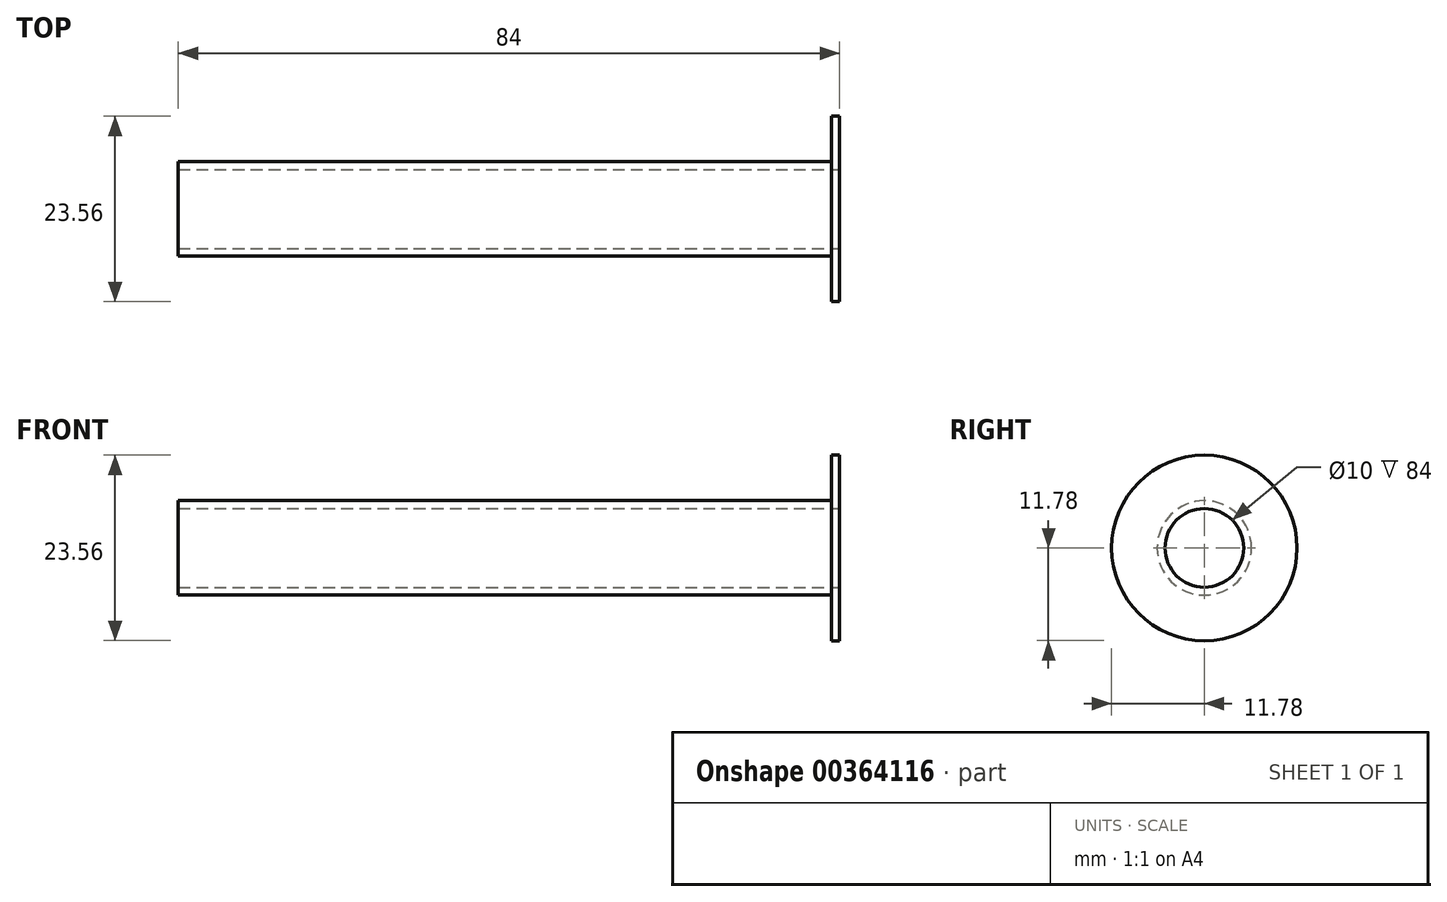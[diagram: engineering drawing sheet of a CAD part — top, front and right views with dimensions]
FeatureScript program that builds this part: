
annotation { "Feature Type Name" : "Feature", "Feature Type Description" : "" }
export const myFeature = defineFeature(function(context is Context, id is Id, definition is map)
    precondition{}
    {
        {
            var Q0;
            Q0=qCreatedBy(makeId("Front.planeOp"),FACE);
            var sketch = newSketch(context, id + "F0", { "sketchPlane" : qUnion([Q0])});
            skLineSegment(sketch, "E0.bottom", {"start": v(0, -5) * mm, "end": v(-42, -5) * mm});
            skLineSegment(sketch, "E0.top", {"start": v(0, -6) * mm, "end": v(-42, -6) * mm});
            skLineSegment(sketch, "E0.left", {"start": v(0, -5) * mm, "end": v(0, -6) * mm});
            skLineSegment(sketch, "E0.right", {"start": v(-42, -5) * mm, "end": v(-42, -6) * mm});
            skLineSegment(sketch, "E1.bottom", {"start": v(-42, -6) * mm, "end": v(-40.95, -6) * mm});
            skLineSegment(sketch, "E1.top", {"start": v(-42, -11.78) * mm, "end": v(-40.95, -11.78) * mm});
            skLineSegment(sketch, "E1.left", {"start": v(-42, -6) * mm, "end": v(-42, -11.78) * mm});
            skLineSegment(sketch, "E1.right", {"start": v(-40.95, -6) * mm, "end": v(-40.95, -11.78) * mm});
            skLineSegment(sketch, "E2.MirrorCS", {"start": v(0, -6) * mm, "end": v(42, -6) * mm});
            skLineSegment(sketch, "E3.MirrorCS", {"start": v(0, -5) * mm, "end": v(42, -5) * mm});
            skLineSegment(sketch, "E4.MirrorCS", {"start": v(42, -5) * mm, "end": v(42, -6) * mm});
            skLineSegment(sketch, "E5.MirrorCS", {"start": v(42, -6) * mm, "end": v(42, -11.78) * mm});
            skLineSegment(sketch, "E6.MirrorCS", {"start": v(40.95, -6) * mm, "end": v(40.95, -11.78) * mm});
            skLineSegment(sketch, "E7.MirrorCS", {"start": v(42, -11.78) * mm, "end": v(40.95, -11.78) * mm});
            skLineSegment(sketch, "E8", {"start": v(0, 0) * mm, "end": v(-10.68, 0) * mm, "construction": true});
            skSolve(sketch);
        }
        {
            var Q0;
            Q0=makeQuery(id+"F0.imprint","IMPRINT",FACE,{"disambiguationData":[TD([[makeQuery(id+"F0.imprint","IMPRINT",EDGE,{"derivedFrom":sQuery(id+"F0.wireOp",EDGE,"E1.bottom")}),-1.0]])]});
            var Q1;
            Q1=makeQuery(id+"F0.imprint","IMPRINT",FACE,{"disambiguationData":[TD([[makeQuery(id+"F0.imprint","IMPRINT",EDGE,{"derivedFrom":sQuery(id+"F0.wireOp",EDGE,"E0.bottom")}),1.0]])]});
            var Q2;
            {var subQ0=sQuery(id+"F0.wireOp",EDGE,"E5.MirrorCS");Q2=makeQuery(id+"F0.imprint","IMPRINT",FACE,{"disambiguationData":[TD([[makeQuery(id+"F0.imprint","IMPRINT",EDGE,{"derivedFrom":subQ0}),-1.0]])]});}
            var Q3;
            {var subQ3=sQuery(id+"F0.wireOp",EDGE,"E0.left");Q3=makeQuery(id+"F0.imprint","IMPRINT",FACE,{"disambiguationData":[TD([[makeQuery(id+"F0.imprint","IMPRINT",EDGE,{"derivedFrom":subQ3}),1.0]])]});}
            var Q4;
            Q4=sQuery(id+"F0.wireOp",EDGE,"E8");
            revolve(context, id + "F1", {"entities" : qUnion([Q0, Q1, Q2, Q3]), "axis" : qUnion([Q4]), "revolveType" : RevolveType.FULL});
        }
    });
